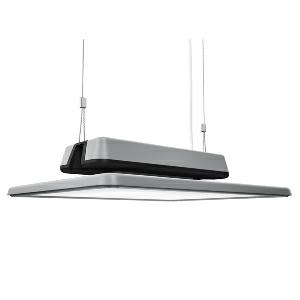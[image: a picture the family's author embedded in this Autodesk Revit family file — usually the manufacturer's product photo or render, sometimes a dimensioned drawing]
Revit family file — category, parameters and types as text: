
# Revit family: acaneo_-_hial_14000_840_w_dali_113547000-00737122_d13e
name_source: partatom
category: Lighting Fixtures
units: mm (PartAtom-declared; Revit-internal decimal feet)

## family parameters
Cut with Voids When Loaded = No
Host = Face
Light Source = No
Part Type = Normal
Room Calculation Point = No
Round Connector Dimension = Use Diameter
Shared = No

## types (1)
- ACANEO - HIAL 14000/840/W/DALI (1 x LED, 15000 lm, 4000K)
    Apparent Load = 90 VA
    Approval mark = CE
    CIE Flux Codes = 76 97 99 100 100
    Color Rendering = 80-89
    Color Temperature = 4000K
    Control Gear = Electronic ballast
    Default Elevation = 1800 mm
    Description = HIAL 14000/840/W/DALI|High bay luminaire|light source: LED|work equipment: Adjustable electronic ballast, digital DALI|connected load: 220-240 V, 50/60 Hz|Power consumption: approx. 90 W|power factor: approx. 0,987|luminous flux: 15000 lm|luminous efficacy: 166 lm/W|colour temperature: Cold white, ca. 4000 K|color rendering index (CRI): >= 80|chromaticity tolerance:  3 SDCM|System of protection: IP 65|class of protection: I|technology: Continuously dimmable|luminaire body|material: Aluminium|surface: Powder coatet|colour: White aluminium|lamp cover: Acrylic (PMMA), Clear|weight (net): approx. 8.2 kg|mains lead: Built-in plug RST 20i5 Einbau|Fastening: Available separately|Accessory: Junction box (RST 20i5)|minimum ambient temperature: -30 ░C|maximum ambient temperature: 70 ░C|glare control: Faceted optic|unified glare rating(4H 8H): <=  22|
    Frequency = 50 Hz, 60 Hz
    Height = 125 mm
    Lamp = 1 x LED
    Lamp Light Flux = 15000 lm
    Lamp count = 1
    Length = 480 mm
    Luminous efficacy = 167 lm/W
    Manufacturer = Waldmann
    ModVariant = No
    Model = 113547000-00737122
    Mounting Place = Ceiling
    Mounting Type = Pendant
    Number of Poles = 1
    OnlyDefault = Yes
    Power Factor = 1
    Product Name = ACANEO - HIAL 14000/840/W/DALI
    Product group = High bay luminaire (industry)
    ProductGroupID = 901
    Protection Class = Protection class I
    Protection Degree = IP 65
    RLX_Detail_Level = 1
    RlxData = <blob elided: 31329 chars, md5=af686d01>
    Socket = socket
    Standby Power = 0 W
    System Light Flux = 15000 lm
    System Power = 90 W
    Type Comments = Product without accessories
    Type Image = acaneo-hial.jpg
    URL = http://relux.com
    VarID = ---
    Voltage = 230 V
    Voltage Range = 110-120 V, 220-240 V
    Weight = 0.00 kg
    Width = 405 mm

## geometry (parser evidence)
native form markers: Blend x4, Sweep x10
no freeform markers — native parametric forms only
